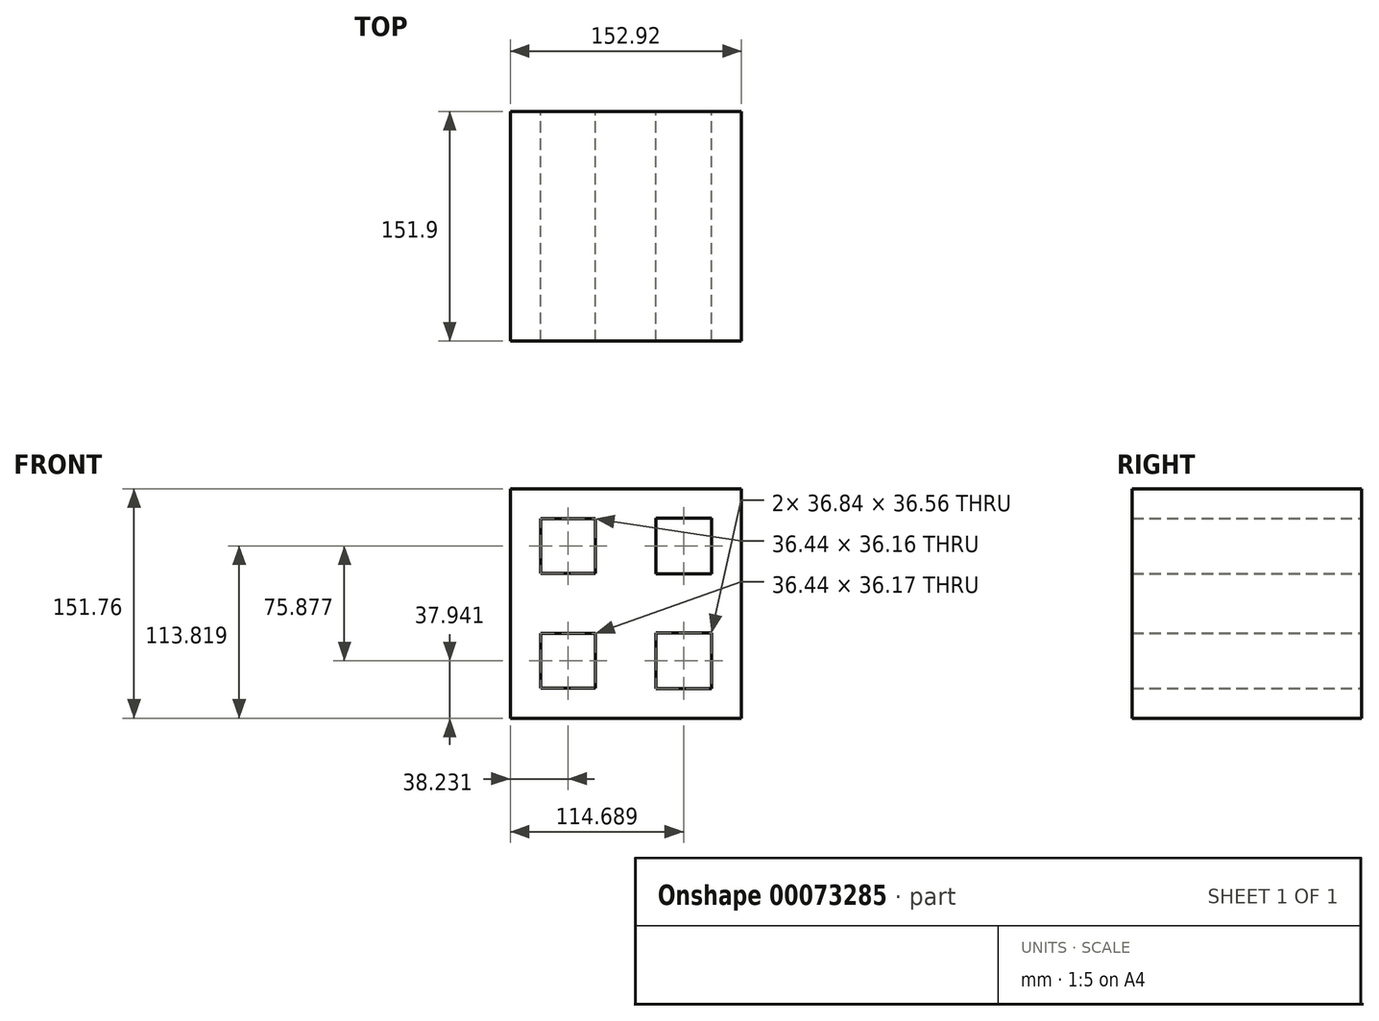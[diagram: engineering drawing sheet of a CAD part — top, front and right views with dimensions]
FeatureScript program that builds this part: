
annotation { "Feature Type Name" : "Feature", "Feature Type Description" : "" }
export const myFeature = defineFeature(function(context is Context, id is Id, definition is map)
    precondition{}
    {
        {
            var Q0;
            Q0=qCreatedBy(makeId("Front.planeOp"),FACE);
            var sketch = newSketch(context, id + "F0", { "sketchPlane" : qUnion([Q0])});
            skLineSegment(sketch, "E0.rect.bottom", {"start": v(-76.46, 75.88) * mm, "end": v(76.46, 75.88) * mm});
            skLineSegment(sketch, "E0.rect.top", {"start": v(-76.46, -75.88) * mm, "end": v(76.46, -75.88) * mm});
            skLineSegment(sketch, "E0.rect.left", {"start": v(-76.46, 75.88) * mm, "end": v(-76.46, -75.88) * mm});
            skLineSegment(sketch, "E0.rect.right", {"start": v(76.46, 75.88) * mm, "end": v(76.46, -75.88) * mm});
            skPoint(sketch, "E0.rect.middle", {"position": v(0, 0) * mm});
            skLineSegment(sketch, "E1", {"start": v(-76.46, 75.88) * mm, "end": v(0, 0) * mm});
            skLineSegment(sketch, "E2", {"start": v(76.46, -75.88) * mm, "end": v(0, 0) * mm});
            skLineSegment(sketch, "E3", {"start": v(76.46, 75.88) * mm, "end": v(0, 0) * mm});
            skLineSegment(sketch, "E4", {"start": v(-76.46, -75.88) * mm, "end": v(0, 0) * mm});
            skLineSegment(sketch, "E5.rect.bottom", {"start": v(-56.45, 56.02) * mm, "end": v(-20, 56.02) * mm});
            skLineSegment(sketch, "E5.rect.top", {"start": v(-56.45, 19.86) * mm, "end": v(-20, 19.86) * mm});
            skLineSegment(sketch, "E5.rect.left", {"start": v(-56.45, 56.02) * mm, "end": v(-56.45, 19.86) * mm});
            skLineSegment(sketch, "E5.rect.right", {"start": v(-20, 56.02) * mm, "end": v(-20, 19.86) * mm});
            skPoint(sketch, "E5.rect.middle", {"position": v(-38.23, 37.94) * mm});
            skLineSegment(sketch, "E6.rect.bottom", {"start": v(56.65, 56.22) * mm, "end": v(19.8, 56.22) * mm});
            skLineSegment(sketch, "E6.rect.top", {"start": v(56.65, 19.66) * mm, "end": v(19.8, 19.66) * mm});
            skLineSegment(sketch, "E6.rect.left", {"start": v(56.65, 56.22) * mm, "end": v(56.65, 19.66) * mm});
            skLineSegment(sketch, "E6.rect.right", {"start": v(19.8, 56.22) * mm, "end": v(19.8, 19.66) * mm});
            skPoint(sketch, "E6.rect.middle", {"position": v(38.23, 37.94) * mm});
            skLineSegment(sketch, "E7.rect.bottom", {"start": v(56.65, -56.22) * mm, "end": v(19.8, -56.22) * mm});
            skLineSegment(sketch, "E7.rect.top", {"start": v(56.65, -19.66) * mm, "end": v(19.8, -19.66) * mm});
            skLineSegment(sketch, "E7.rect.left", {"start": v(56.65, -56.22) * mm, "end": v(56.65, -19.66) * mm});
            skLineSegment(sketch, "E7.rect.right", {"start": v(19.8, -56.22) * mm, "end": v(19.8, -19.66) * mm});
            skPoint(sketch, "E7.rect.middle", {"position": v(38.23, -37.94) * mm});
            skLineSegment(sketch, "E8.rect.bottom", {"start": v(-56.45, -56.02) * mm, "end": v(-20, -56.02) * mm});
            skLineSegment(sketch, "E8.rect.top", {"start": v(-56.45, -19.86) * mm, "end": v(-20, -19.86) * mm});
            skLineSegment(sketch, "E8.rect.left", {"start": v(-56.45, -56.02) * mm, "end": v(-56.45, -19.86) * mm});
            skLineSegment(sketch, "E8.rect.right", {"start": v(-20, -56.02) * mm, "end": v(-20, -19.86) * mm});
            skPoint(sketch, "E8.rect.middle", {"position": v(-38.23, -37.94) * mm});
            skSolve(sketch);
        }
        {
            var Q0;
            {var subQ1=sQuery(id+"F0.wireOp",EDGE,"E0.rect.bottom");Q0=makeQuery(id+"F0.imprint","IMPRINT",FACE,{"disambiguationData":[TD([[makeQuery(id+"F0.imprint","IMPRINT",EDGE,{"derivedFrom":subQ1}),-1.0]])]});}
            var Q1;
            {var subQ1=sQuery(id+"F0.wireOp",EDGE,"E0.rect.left");Q1=makeQuery(id+"F0.imprint","IMPRINT",FACE,{"disambiguationData":[TD([[makeQuery(id+"F0.imprint","IMPRINT",EDGE,{"derivedFrom":subQ1}),1.0]])]});}
            var Q2;
            {var subQ1=sQuery(id+"F0.wireOp",EDGE,"E0.rect.top");Q2=makeQuery(id+"F0.imprint","IMPRINT",FACE,{"disambiguationData":[TD([[makeQuery(id+"F0.imprint","IMPRINT",EDGE,{"derivedFrom":subQ1}),1.0]])]});}
            var Q3;
            {var subQ1=sQuery(id+"F0.wireOp",EDGE,"E0.rect.right");Q3=makeQuery(id+"F0.imprint","IMPRINT",FACE,{"disambiguationData":[TD([[makeQuery(id+"F0.imprint","IMPRINT",EDGE,{"derivedFrom":subQ1}),-1.0]])]});}
            extrude(context, id + "F1", {"entities" : qUnion([Q0, Q1, Q2, Q3]), "endBound" : BoundingType.SYMMETRIC, "depth" : 151.9 * mm});
        }
    });
